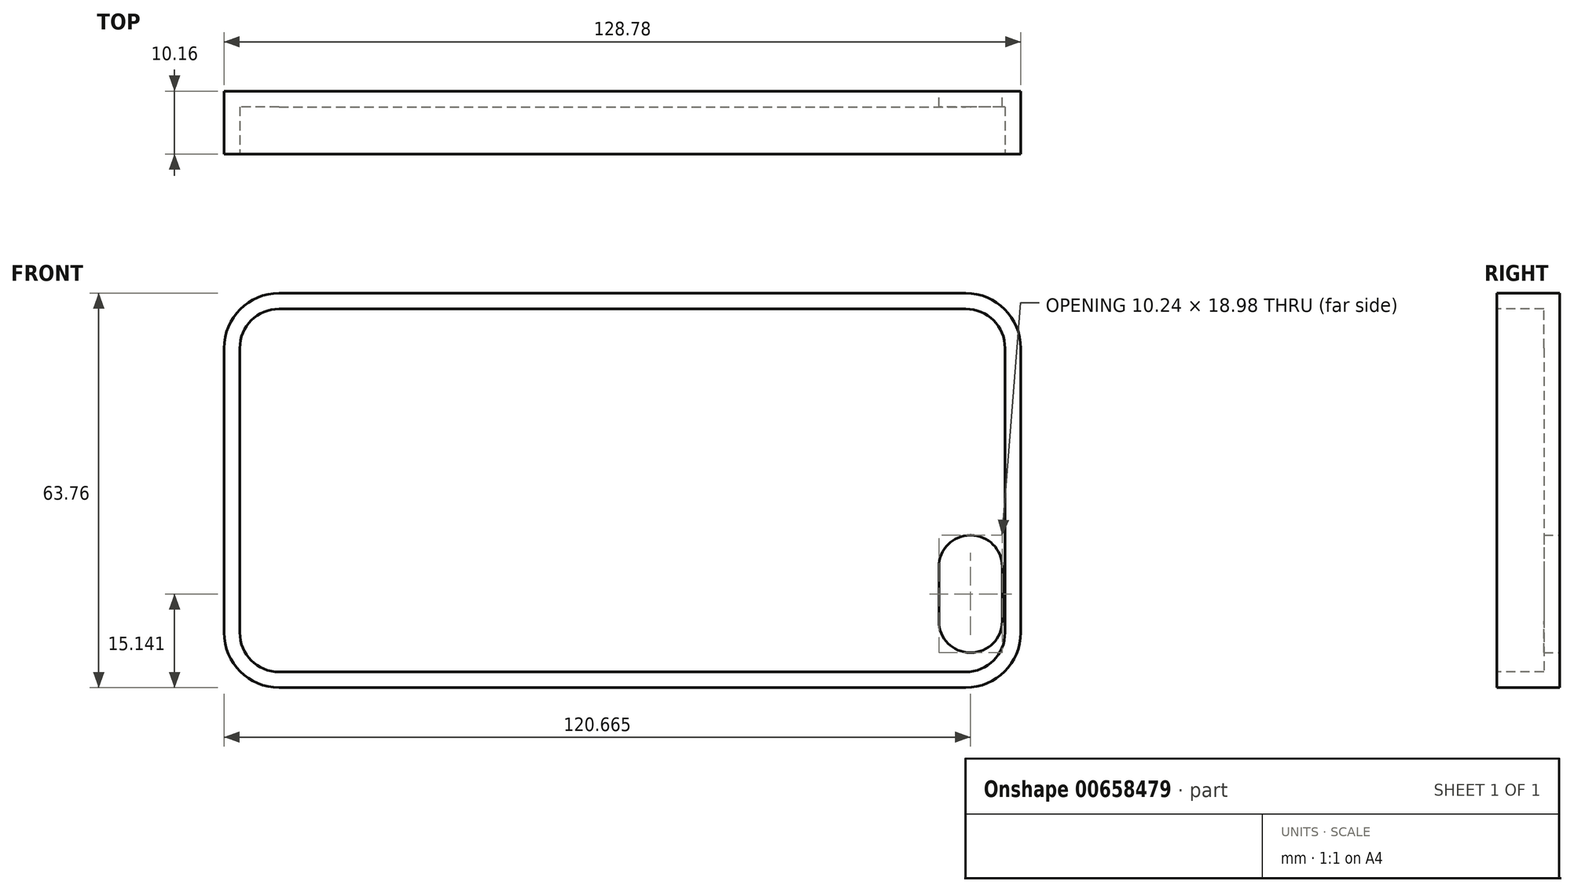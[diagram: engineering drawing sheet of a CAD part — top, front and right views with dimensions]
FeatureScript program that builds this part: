
annotation { "Feature Type Name" : "Feature", "Feature Type Description" : "" }
export const myFeature = defineFeature(function(context is Context, id is Id, definition is map)
    precondition{}
    {
        {
            var Q0;
            Q0=qCreatedBy(makeId("Front.planeOp"),FACE);
            var sketch = newSketch(context, id + "F0", { "sketchPlane" : qUnion([Q0])});
            skLineSegment(sketch, "E0.bottom", {"start": v(-55.5, 31.88) * mm, "end": v(55.5, 31.88) * mm});
            skLineSegment(sketch, "E0.top", {"start": v(-55.5, -31.88) * mm, "end": v(55.5, -31.88) * mm});
            skLineSegment(sketch, "E0.left", {"start": v(-64.39, 22.99) * mm, "end": v(-64.39, -22.99) * mm});
            skLineSegment(sketch, "E0.right", {"start": v(64.39, 22.99) * mm, "end": v(64.39, -22.99) * mm});
            skPoint(sketch, "E0.middle", {"position": v(0, 0) * mm});
            skPoint(sketch, "E1.visualSharp", {"position": v(-64.39, 31.88) * mm});
            skArc(sketch, "E1.filletArc", {"start": v(-55.5, 31.88) * mm, "mid": v(-61.79, 29.27) * mm, "end": v(-64.39, 22.99) * mm});
            skPoint(sketch, "E2.visualSharp", {"position": v(64.39, 31.88) * mm});
            skArc(sketch, "E2.filletArc", {"start": v(64.39, 22.99) * mm, "mid": v(61.79, 29.27) * mm, "end": v(55.5, 31.88) * mm});
            skPoint(sketch, "E3.visualSharp", {"position": v(64.39, -31.88) * mm});
            skArc(sketch, "E3.filletArc", {"start": v(55.5, -31.88) * mm, "mid": v(61.79, -29.27) * mm, "end": v(64.39, -22.99) * mm});
            skPoint(sketch, "E4.visualSharp", {"position": v(-64.39, -31.88) * mm});
            skArc(sketch, "E4.filletArc", {"start": v(-64.39, -22.99) * mm, "mid": v(-61.79, -29.27) * mm, "end": v(-55.5, -31.88) * mm});
            skSolve(sketch);
        }
        {
            var Q0;
            Q0=makeQuery(id+"F0.imprint","IMPRINT",FACE,{"disambiguationData":[TD([[makeQuery(id+"F0.imprint","IMPRINT",EDGE,{"derivedFrom":sQuery(id+"F0.wireOp",EDGE,"E0.bottom")}),-1.0]])]});
            extrude(context, id + "F1", {"entities" : qUnion([Q0]), "depth" : 10.16 * mm, "offsetDistance" : 25.4 * mm});
        }
        {
            var Q0;
            Q0=makeQuery(id+"F1.opExtrude","CAP_FACE",FACE,{"disambiguationData":[OSD([sQuery(id+"F0.wireOp",EDGE,"E0.bottom"),sQuery(id+"F0.wireOp",EDGE,"E0.top"),sQuery(id+"F0.wireOp",EDGE,"E0.left"),sQuery(id+"F0.wireOp",EDGE,"E0.right"),sQuery(id+"F0.wireOp",EDGE,"E1.filletArc"),sQuery(id+"F0.wireOp",EDGE,"E2.filletArc"),sQuery(id+"F0.wireOp",EDGE,"E3.filletArc"),sQuery(id+"F0.wireOp",EDGE,"E4.filletArc")])],"isStart":false});
            var sketch = newSketch(context, id + "F2", { "sketchPlane" : qUnion([Q0])});
            skLineSegment(sketch, "E5.bottom", {"start": v(-55.5, 29.34) * mm, "end": v(55.5, 29.34) * mm});
            skLineSegment(sketch, "E5.top", {"start": v(-55.5, -29.34) * mm, "end": v(55.5, -29.34) * mm});
            skLineSegment(sketch, "E5.left", {"start": v(-61.85, 22.99) * mm, "end": v(-61.85, -22.99) * mm});
            skLineSegment(sketch, "E5.right", {"start": v(61.85, 22.99) * mm, "end": v(61.85, -22.99) * mm});
            skPoint(sketch, "E5.middle", {"position": v(0, 0) * mm});
            skPoint(sketch, "E6.visualSharp", {"position": v(-61.85, 29.34) * mm});
            skArc(sketch, "E6.filletArc", {"start": v(-55.5, 29.34) * mm, "mid": v(-59.99, 27.48) * mm, "end": v(-61.85, 22.99) * mm});
            skPoint(sketch, "E7.visualSharp", {"position": v(61.85, 29.34) * mm});
            skArc(sketch, "E7.filletArc", {"start": v(61.85, 22.99) * mm, "mid": v(59.99, 27.48) * mm, "end": v(55.5, 29.34) * mm});
            skPoint(sketch, "E8.visualSharp", {"position": v(61.85, -29.34) * mm});
            skArc(sketch, "E8.filletArc", {"start": v(55.5, -29.34) * mm, "mid": v(59.99, -27.48) * mm, "end": v(61.85, -22.99) * mm});
            skPoint(sketch, "E9.visualSharp", {"position": v(-61.85, -29.34) * mm});
            skArc(sketch, "E9.filletArc", {"start": v(-61.85, -22.99) * mm, "mid": v(-59.99, -27.48) * mm, "end": v(-55.5, -29.34) * mm});
            skSolve(sketch);
        }
        {
            var Q0;
            Q0=makeQuery(id+"F2.imprint","IMPRINT",FACE,{"disambiguationData":[TD([[makeQuery(id+"F2.imprint","IMPRINT",EDGE,{"derivedFrom":sQuery(id+"F2.wireOp",EDGE,"E5.bottom")}),-1.0]])]});
            extrude(context, id + "F3", {"entities" : qUnion([Q0]), "operationType" : NewBodyOperationType.REMOVE, "oppositeDirection" : true, "depth" : 7.62 * mm, "offsetDistance" : 25.4 * mm});
        }
        {
            var Q0;
            Q0=makeQuery(id+"F1.opExtrude","CAP_FACE",FACE,{"disambiguationData":[OSD([sQuery(id+"F0.wireOp",EDGE,"E0.bottom"),sQuery(id+"F0.wireOp",EDGE,"E0.top"),sQuery(id+"F0.wireOp",EDGE,"E0.left"),sQuery(id+"F0.wireOp",EDGE,"E0.right"),sQuery(id+"F0.wireOp",EDGE,"E1.filletArc"),sQuery(id+"F0.wireOp",EDGE,"E2.filletArc"),sQuery(id+"F0.wireOp",EDGE,"E3.filletArc"),sQuery(id+"F0.wireOp",EDGE,"E4.filletArc")])],"isStart":true});
            var sketch = newSketch(context, id + "F4", { "sketchPlane" : qUnion([Q0])});
            skLineSegment(sketch, "E10.bottom", {"start": v(-56.31, -26.23) * mm, "end": v(-56.24, -26.23) * mm});
            skLineSegment(sketch, "E10.top", {"start": v(-56.31, -7.25) * mm, "end": v(-56.24, -7.25) * mm});
            skLineSegment(sketch, "E10.left", {"start": v(-61.4, -21.15) * mm, "end": v(-61.4, -12.33) * mm});
            skLineSegment(sketch, "E10.right", {"start": v(-51.16, -21.15) * mm, "end": v(-51.16, -12.33) * mm});
            skPoint(sketch, "E11.visualSharp", {"position": v(-61.4, -7.25) * mm});
            skArc(sketch, "E11.filletArc", {"start": v(-56.31, -7.25) * mm, "mid": v(-59.9, -8.74) * mm, "end": v(-61.4, -12.33) * mm});
            skPoint(sketch, "E12.visualSharp", {"position": v(-51.16, -26.23) * mm});
            skArc(sketch, "E12.filletArc", {"start": v(-56.24, -26.23) * mm, "mid": v(-52.64, -24.74) * mm, "end": v(-51.16, -21.15) * mm});
            skPoint(sketch, "E13.visualSharp", {"position": v(-51.16, -7.25) * mm});
            skArc(sketch, "E13.filletArc", {"start": v(-51.16, -12.33) * mm, "mid": v(-52.64, -8.74) * mm, "end": v(-56.24, -7.25) * mm});
            skPoint(sketch, "E14.visualSharp", {"position": v(-61.4, -26.23) * mm});
            skArc(sketch, "E14.filletArc", {"start": v(-61.4, -21.15) * mm, "mid": v(-59.9, -24.74) * mm, "end": v(-56.31, -26.23) * mm});
            skSolve(sketch);
        }
        {
            var Q0;
            Q0 = qSketchRegion(id + "F4", true);
            extrude(context, id + "F5", {"entities" : qUnion([Q0]), "operationType" : NewBodyOperationType.REMOVE, "oppositeDirection" : true, "depth" : 25.4 * mm, "offsetDistance" : 25.4 * mm});
        }
    });
